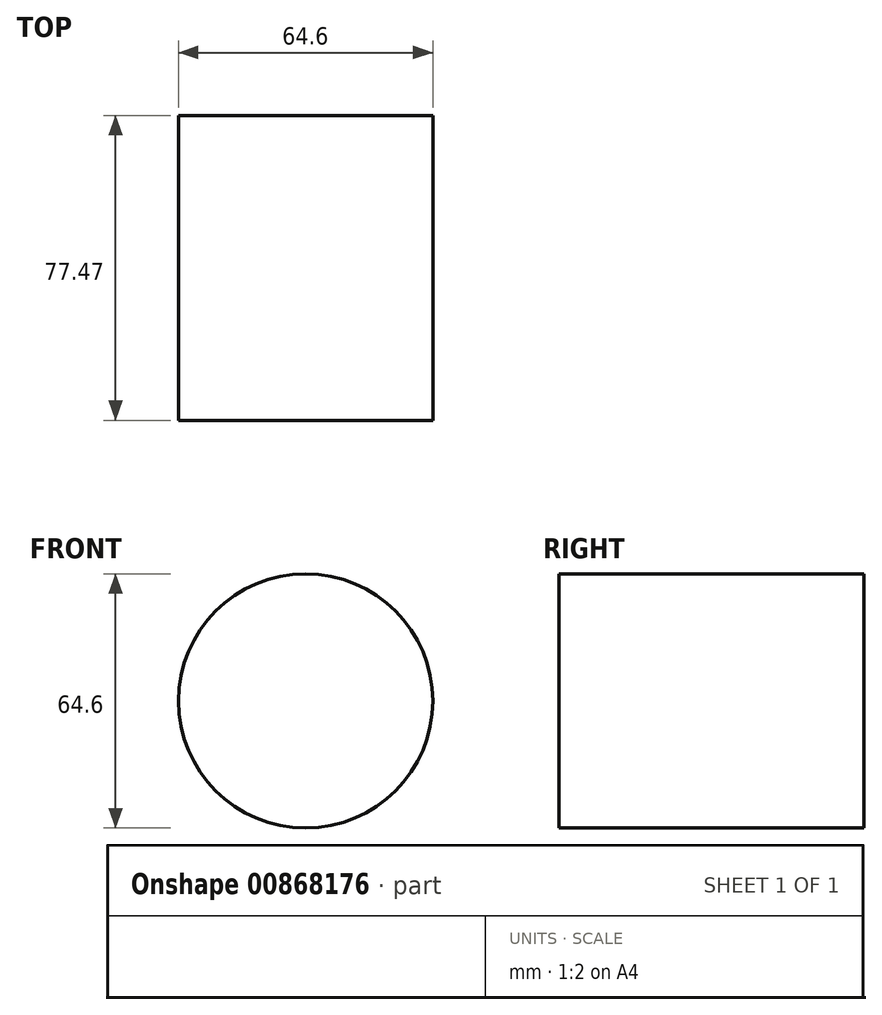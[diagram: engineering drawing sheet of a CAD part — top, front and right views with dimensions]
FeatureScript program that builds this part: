
annotation { "Feature Type Name" : "Feature", "Feature Type Description" : "" }
export const myFeature = defineFeature(function(context is Context, id is Id, definition is map)
    precondition{}
    {
        {
            var Q0;
            Q0=qCreatedBy(makeId("Front.planeOp"),FACE);
            var sketch = newSketch(context, id + "F0", { "sketchPlane" : qUnion([Q0])});
            skCircle(sketch, "E0", {"center": v(0, 0) * mm, "radius": 32.3 * mm});
            skSolve(sketch);
        }
        {
            var Q0;
            Q0=makeQuery(id+"F0.imprint","IMPRINT",FACE,{"disambiguationData":[TD([[makeQuery(id+"F0.imprint","IMPRINT",EDGE,{"derivedFrom":sQuery(id+"F0.wireOp",EDGE,"E0")}),1.0]])]});
            extrude(context, id + "F1", {"entities" : qUnion([Q0]), "depth" : 77.47 * mm, "offsetDistance" : 25.4 * mm});
        }
    });
